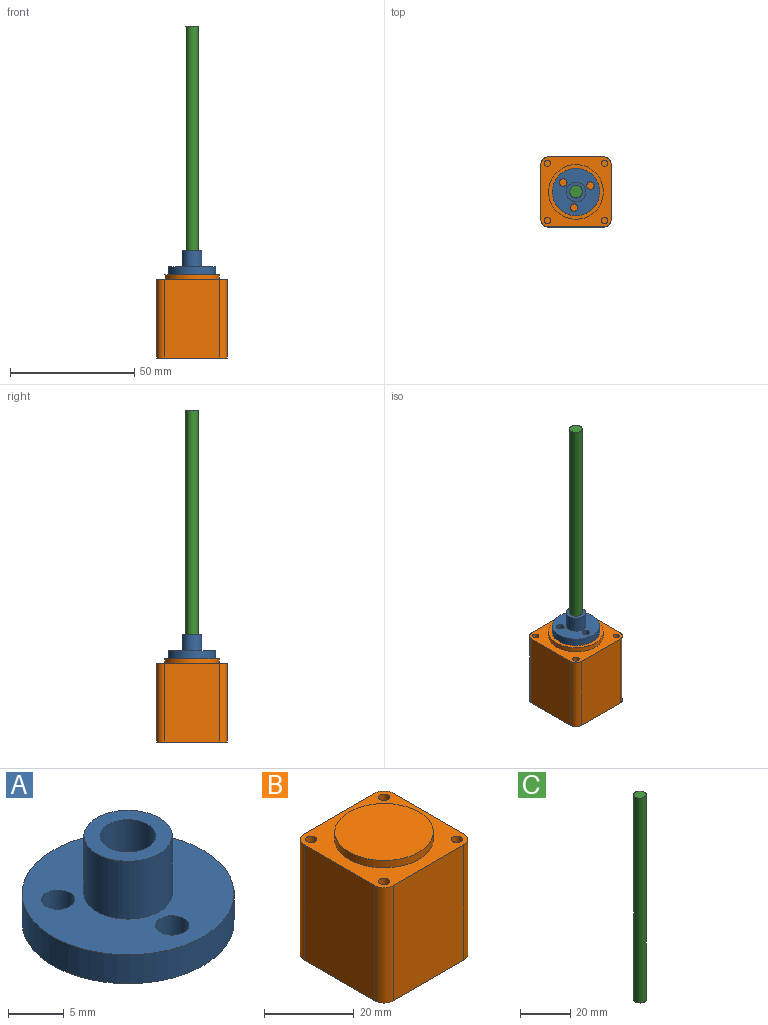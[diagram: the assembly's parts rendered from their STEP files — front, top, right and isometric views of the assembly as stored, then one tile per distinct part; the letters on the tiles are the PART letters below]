
ASSEMBLY  parts=3 mates=2
PART A: 9 faces, bbox 19.1x19.1x9.5 mm
  f0: cylinder r=2.5mm len=9.53mm, axis (0,0,-1), area 149.7mm2, adj f3,f5
  f1: cylinder r=9.53mm len=19.05mm, axis (0,0,-1), area 190.3mm2, adj f2,f3
  f2: plane 19.05x19.05mm, normal (0,0,1), area 214.3mm2, adj f1,f4,f6,f7,f8
  f3: plane 19.05x19.05mm, normal (0,0,-1), area 244.2mm2, adj f0,f1,f6,f7,f8
  f4: cylinder r=3.97mm len=7.94mm, axis (0,0,-1), area 158.4mm2, adj f2,f5
  f5: plane 7.94x7.94mm, normal (0,0,1), area 29.9mm2, adj f0,f4
  f6: cylinder r=1.5mm len=3.18mm, axis (0,0,-1), area 30mm2, adj f2,f3
  f7: cylinder r=1.5mm len=3.18mm, axis (0,0,-1), area 30mm2, adj f2,f3
  f8: cylinder r=1.5mm len=3.18mm, axis (0,0,-1), area 30mm2, adj f2,f3
PART B: 20 faces, bbox 28.2x28.2x33.5 mm
  f0: plane 28.2x28.2mm, normal (0,0,1), area 387.7mm2, adj f1,f3,f4,f5,f6,f8,f10,f12
  f1: plane 31.5x22.2mm, normal (-1,0,0), area 699.3mm2, adj f0,f2,f17,f19
  f2: plane 28.2x28.2mm, normal (0,0,-1), area 787.5mm2, adj f1,f3,f4,f5,f16,f17,f18,f19
  f3: plane 31.5x22.2mm, normal (1,0,0), area 699.3mm2, adj f0,f2,f16,f18
  f4: plane 31.5x22.2mm, normal (0,-1,0), area 699.3mm2, adj f0,f2,f18,f19
  f5: plane 31.5x22.2mm, normal (0,1,0), area 699.3mm2, adj f0,f2,f16,f17
  f6: cylinder r=1.25mm len=3.5mm, axis (0,0,1), area 27.5mm2, adj f0,f7
  f7: plane 2.5x2.5mm, normal (0,0,1), area 4.9mm2, adj f6
  f8: cylinder r=1.25mm len=3.5mm, axis (0,0,1), area 27.5mm2, adj f0,f9
  f9: plane 2.5x2.5mm, normal (0,0,1), area 4.9mm2, adj f8
  f10: cylinder r=1.25mm len=3.5mm, axis (0,0,1), area 27.5mm2, adj f0,f11
  f11: plane 2.5x2.5mm, normal (0,0,1), area 4.9mm2, adj f10
  f12: cylinder r=1.25mm len=3.5mm, axis (0,0,1), area 27.5mm2, adj f0,f13
  f13: plane 2.5x2.5mm, normal (0,0,1), area 4.9mm2, adj f12
  f14: cylinder r=11mm len=22mm, axis (0,0,-1), area 138.2mm2, adj f0,f15
  f15: plane 22x22mm, normal (0,0,1), area 380.1mm2, adj f14
  f16: cylinder r=3mm len=31.5mm, axis (0,0,1), area 148.4mm2, adj f0,f2,f3,f5
  f17: cylinder r=3mm len=31.5mm, axis (0,0,-1), area 148.4mm2, adj f0,f1,f2,f5
  f18: cylinder r=3mm len=31.5mm, axis (0,0,-1), area 148.4mm2, adj f0,f2,f3,f4
  f19: cylinder r=3mm len=31.5mm, axis (0,0,1), area 148.4mm2, adj f0,f1,f2,f4
PART C: 3 faces, bbox 5x5x100 mm
  f0: cylinder r=2.5mm len=100mm, axis (0,0,-1), area 1570.8mm2, adj f1,f2
  f1: plane 5x5mm, normal (0,0,1), area 19.6mm2, adj f0
  f2: plane 5x5mm, normal (0,0,-1), area 19.6mm2, adj f0
PLACE A t=(-22.01,27.76,23.95)mm
PLACE B t=(-22.01,27.76,23.95)mm fixed
PLACE C t=(-22.01,27.76,25.95)mm
MATE slider A.f0 <-> C.f0  axis (0,0,-1) through (-22.01,27.76,25.95)mm
MATE fastened C.f0 <-> B.f14  axis (0,0,-1) through (-22.01,27.76,25.95)mm
